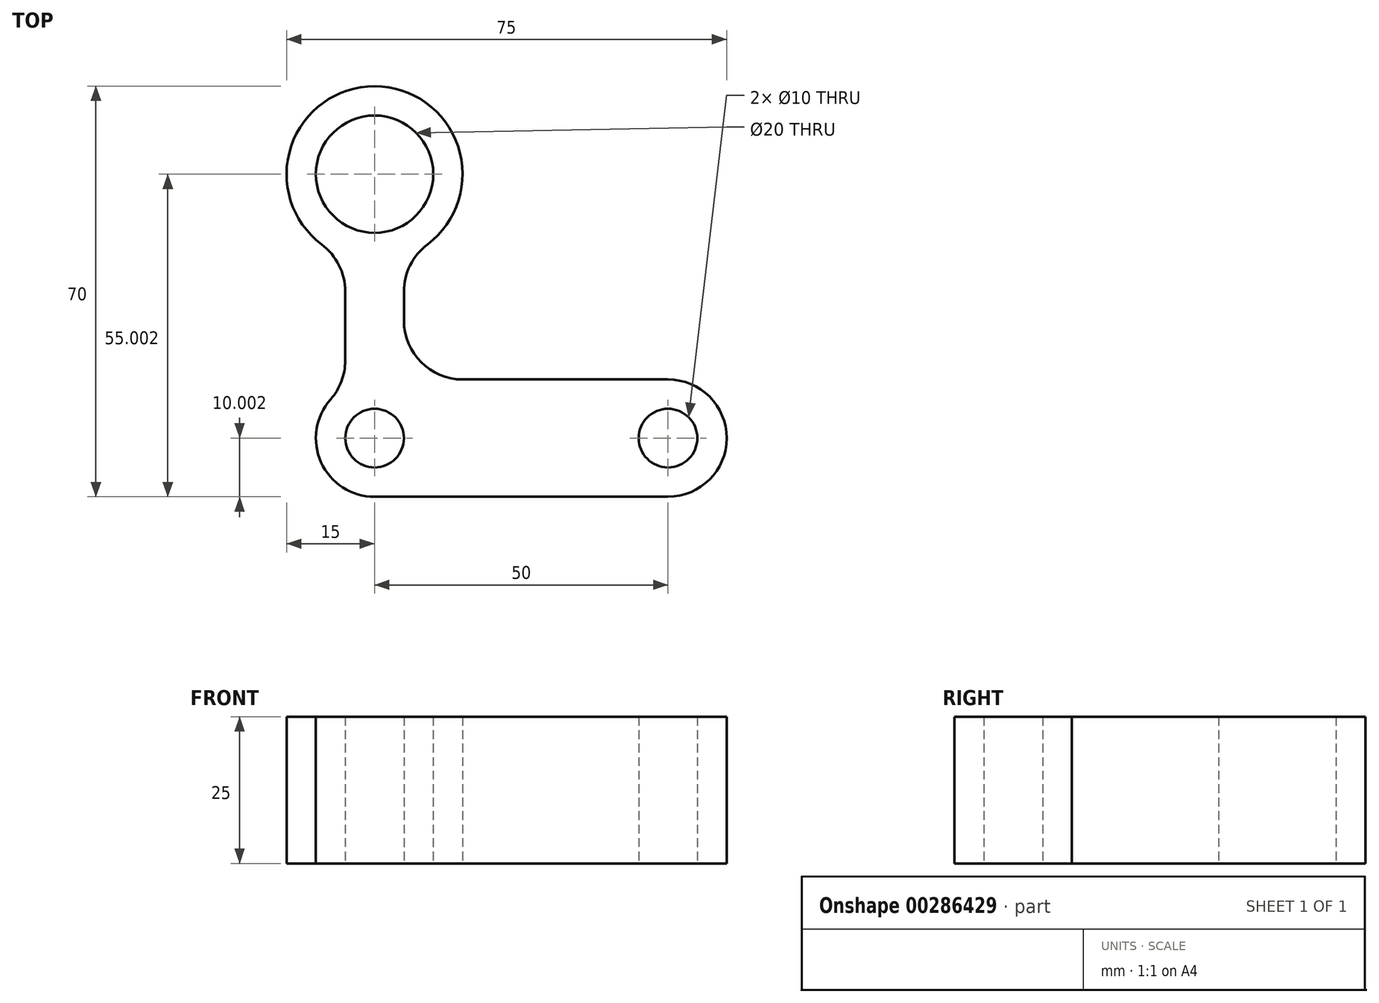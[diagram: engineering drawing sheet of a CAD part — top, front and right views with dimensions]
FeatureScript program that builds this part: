
annotation { "Feature Type Name" : "Feature", "Feature Type Description" : "" }
export const myFeature = defineFeature(function(context is Context, id is Id, definition is map)
    precondition{}
    {
        {
            var Q0;
            Q0=qCreatedBy(makeId("Top.planeOp"),FACE);
            var sketch = newSketch(context, id + "F0", { "sketchPlane" : qUnion([Q0])});
            skLineSegment(sketch, "E0", {"start": v(-36.92, -35.89) * mm, "end": v(13.08, -35.89) * mm});
            skArc(sketch, "E1", {"start": v(13.08, -35.89) * mm, "mid": v(23.08, -25.89) * mm, "end": v(13.08, -15.89) * mm});
            skCircle(sketch, "E2", {"center": v(13.08, -25.89) * mm, "radius": 5 * mm});
            skArc(sketch, "E3", {"start": v(-44.42, -19.27) * mm, "mid": v(-46.03, -30) * mm, "end": v(-36.92, -35.89) * mm});
            skCircle(sketch, "E4", {"center": v(-36.92, -25.89) * mm, "radius": 5 * mm});
            skLineSegment(sketch, "E5", {"start": v(-31.92, -25.89) * mm, "end": v(8.08, -25.89) * mm});
            skLineSegment(sketch, "E6", {"start": v(-31.92, -5.89) * mm, "end": v(-31.92, -0.89) * mm});
            skLineSegment(sketch, "E7", {"start": v(-41.92, -12.66) * mm, "end": v(-41.92, -0.89) * mm});
            skPoint(sketch, "E8.orphan", {"position": v(-41.92, -25.89) * mm});
            skLineSegment(sketch, "E9", {"start": v(13.08, -15.89) * mm, "end": v(-21.92, -15.89) * mm});
            skPoint(sketch, "E10", {"position": v(-36.92, 19.11) * mm});
            skArc(sketch, "E11", {"start": v(-27.92, 7.11) * mm, "mid": v(-36.92, 34.11) * mm, "end": v(-45.92, 7.11) * mm});
            skCircle(sketch, "E12", {"center": v(-36.92, 19.11) * mm, "radius": 10 * mm});
            skArc(sketch, "E13.filletArc", {"start": v(-27.92, 7.11) * mm, "mid": v(-30.86, 3.58) * mm, "end": v(-31.92, -0.89) * mm});
            skArc(sketch, "E14.filletArc", {"start": v(-41.92, -0.89) * mm, "mid": v(-42.98, 3.58) * mm, "end": v(-45.92, 7.11) * mm});
            skArc(sketch, "E15.filletArc", {"start": v(-44.42, -19.27) * mm, "mid": v(-42.57, -16.2) * mm, "end": v(-41.92, -12.66) * mm});
            skArc(sketch, "E16.filletArc", {"start": v(-31.92, -5.89) * mm, "mid": v(-29, -12.96) * mm, "end": v(-21.92, -15.89) * mm});
            skSolve(sketch);
        }
        {
            var Q0;
            Q0 = qSketchRegion(id + "F0", true);
            extrude(context, id + "F1", {"entities" : qUnion([Q0]), "depth" : 25 * mm});
        }
    });
